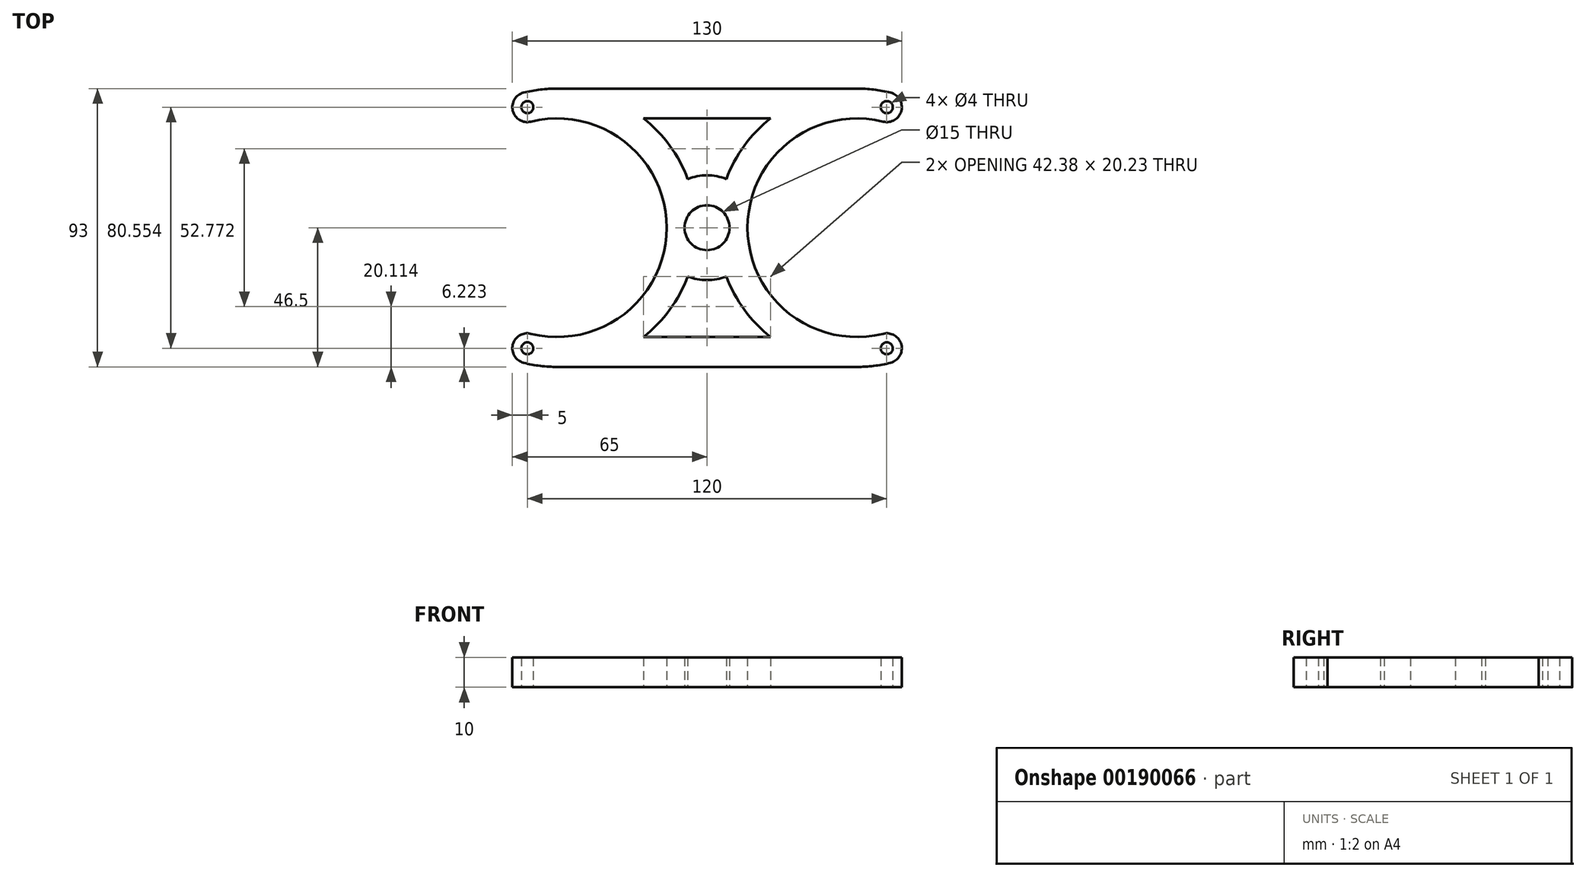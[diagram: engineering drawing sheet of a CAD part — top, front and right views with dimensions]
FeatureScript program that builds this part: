
annotation { "Feature Type Name" : "Feature", "Feature Type Description" : "" }
export const myFeature = defineFeature(function(context is Context, id is Id, definition is map)
    precondition{}
    {
        {
            var Q0;
            Q0=qCreatedBy(makeId("Top.planeOp"),FACE);
            var sketch = newSketch(context, id + "F0", { "sketchPlane" : qUnion([Q0])});
            skArc(sketch, "E0", {"start": v(0, -7.5) * mm, "mid": v(7.5, 0) * mm, "end": v(0, 7.5) * mm});
            skLineSegment(sketch, "E1", {"start": v(0, 0) * mm, "end": v(50, 0) * mm, "construction": true});
            skArc(sketch, "E2", {"start": v(60, 35.1) * mm, "mid": v(13.5, 0) * mm, "end": v(60, -35.1) * mm});
            skArc(sketch, "E3.0", {"start": v(6.44, 16.27) * mm, "mid": v(3.28, 17.2) * mm, "end": v(0, 17.5) * mm});
            skArc(sketch, "E4.0", {"start": v(6.44, -16.27) * mm, "mid": v(12.43, -27.4) * mm, "end": v(21.2, -36.5) * mm});
            skLineSegment(sketch, "E5", {"start": v(50, 46.5) * mm, "end": v(0, 46.5) * mm});
            skLineSegment(sketch, "E6", {"start": v(21.2, 36.5) * mm, "end": v(0, 36.5) * mm});
            skLineSegment(sketch, "E7", {"start": v(50, 0) * mm, "end": v(60, 40.28) * mm, "construction": true});
            skArc(sketch, "E8", {"start": v(58.8, 35.42) * mm, "mid": v(64.85, 39.07) * mm, "end": v(61.2, 45.13) * mm});
            skLineSegment(sketch, "E9", {"start": v(50, 0) * mm, "end": v(60, -40.28) * mm, "construction": true});
            skArc(sketch, "E10", {"start": v(61.2, -45.13) * mm, "mid": v(64.85, -39.07) * mm, "end": v(58.8, -35.42) * mm});
            skLineSegment(sketch, "E11", {"start": v(60, 40.28) * mm, "end": v(60, -40.28) * mm, "construction": true});
            skArc(sketch, "E12.trimOffspring", {"start": v(61.2, 45.13) * mm, "mid": v(55.64, 46.16) * mm, "end": v(50, 46.5) * mm});
            skLineSegment(sketch, "E13", {"start": v(50, -46.5) * mm, "end": v(0, -46.5) * mm});
            skLineSegment(sketch, "E14", {"start": v(21.2, -36.5) * mm, "end": v(0, -36.5) * mm});
            skLineSegment(sketch, "E15", {"start": v(0, 46.5) * mm, "end": v(0, -46.5) * mm, "construction": true});
            skArc(sketch, "E16.trimOffspring", {"start": v(0, -17.5) * mm, "mid": v(3.28, -17.2) * mm, "end": v(6.44, -16.27) * mm});
            skArc(sketch, "E17.trimOffspring", {"start": v(50, -46.5) * mm, "mid": v(55.64, -46.16) * mm, "end": v(61.2, -45.13) * mm});
            skArc(sketch, "E18.trimOffspring", {"start": v(21.2, 36.5) * mm, "mid": v(12.43, 27.4) * mm, "end": v(6.44, 16.27) * mm});
            skLineSegment(sketch, "E19.MirrorCS", {"start": v(-21.2, 36.5) * mm, "end": v(0, 36.5) * mm});
            skLineSegment(sketch, "E20.MirrorCS", {"start": v(-50, 46.5) * mm, "end": v(0, 46.5) * mm});
            skArc(sketch, "E21.MirrorCS", {"start": v(-61.2, 45.13) * mm, "mid": v(-55.64, 46.16) * mm, "end": v(-50, 46.5) * mm});
            skArc(sketch, "E22.MirrorCS", {"start": v(-58.8, 35.42) * mm, "mid": v(-64.85, 39.07) * mm, "end": v(-61.2, 45.13) * mm});
            skArc(sketch, "E23.MirrorCS", {"start": v(-60, 35.1) * mm, "mid": v(-13.5, 0) * mm, "end": v(-60, -35.1) * mm});
            skArc(sketch, "E24.MirrorCS", {"start": v(-61.2, -45.13) * mm, "mid": v(-64.85, -39.07) * mm, "end": v(-58.8, -35.42) * mm});
            skArc(sketch, "E25.MirrorCS", {"start": v(-50, -46.5) * mm, "mid": v(-55.64, -46.16) * mm, "end": v(-61.2, -45.13) * mm});
            skLineSegment(sketch, "E26.MirrorCS", {"start": v(-50, -46.5) * mm, "end": v(0, -46.5) * mm});
            skLineSegment(sketch, "E27.MirrorCS", {"start": v(-21.2, -36.5) * mm, "end": v(0, -36.5) * mm});
            skArc(sketch, "E28.MirrorCS", {"start": v(-6.44, -16.27) * mm, "mid": v(-12.43, -27.4) * mm, "end": v(-21.2, -36.5) * mm});
            skArc(sketch, "E29.MirrorCS", {"start": v(0, -17.5) * mm, "mid": v(-3.28, -17.2) * mm, "end": v(-6.44, -16.27) * mm});
            skArc(sketch, "E30.MirrorCS", {"start": v(0, -7.5) * mm, "mid": v(-7.5, 0) * mm, "end": v(0, 7.5) * mm});
            skArc(sketch, "E31.MirrorCS", {"start": v(-6.44, 16.27) * mm, "mid": v(-3.28, 17.2) * mm, "end": v(0, 17.5) * mm});
            skArc(sketch, "E32.MirrorCS", {"start": v(-21.2, 36.5) * mm, "mid": v(-12.43, 27.4) * mm, "end": v(-6.44, 16.27) * mm});
            skCircle(sketch, "E33", {"center": v(-60, 40.28) * mm, "radius": 2 * mm});
            skCircle(sketch, "E34", {"center": v(-60, -40.28) * mm, "radius": 2 * mm});
            skCircle(sketch, "E35", {"center": v(60, -40.28) * mm, "radius": 2 * mm});
            skCircle(sketch, "E36", {"center": v(60, 40.28) * mm, "radius": 2 * mm});
            skSolve(sketch);
        }
        {
            var Q0;
            Q0=makeQuery(id+"F0.imprint","IMPRINT",FACE,{"disambiguationData":[TD([[makeQuery(id+"F0.imprint","IMPRINT",EDGE,{"derivedFrom":sQuery(id+"F0.wireOp",EDGE,"E0")}),-1.0]])]});
            extrude(context, id + "F1", {"entities" : qUnion([Q0]), "depth" : 10 * mm});
        }
    });
